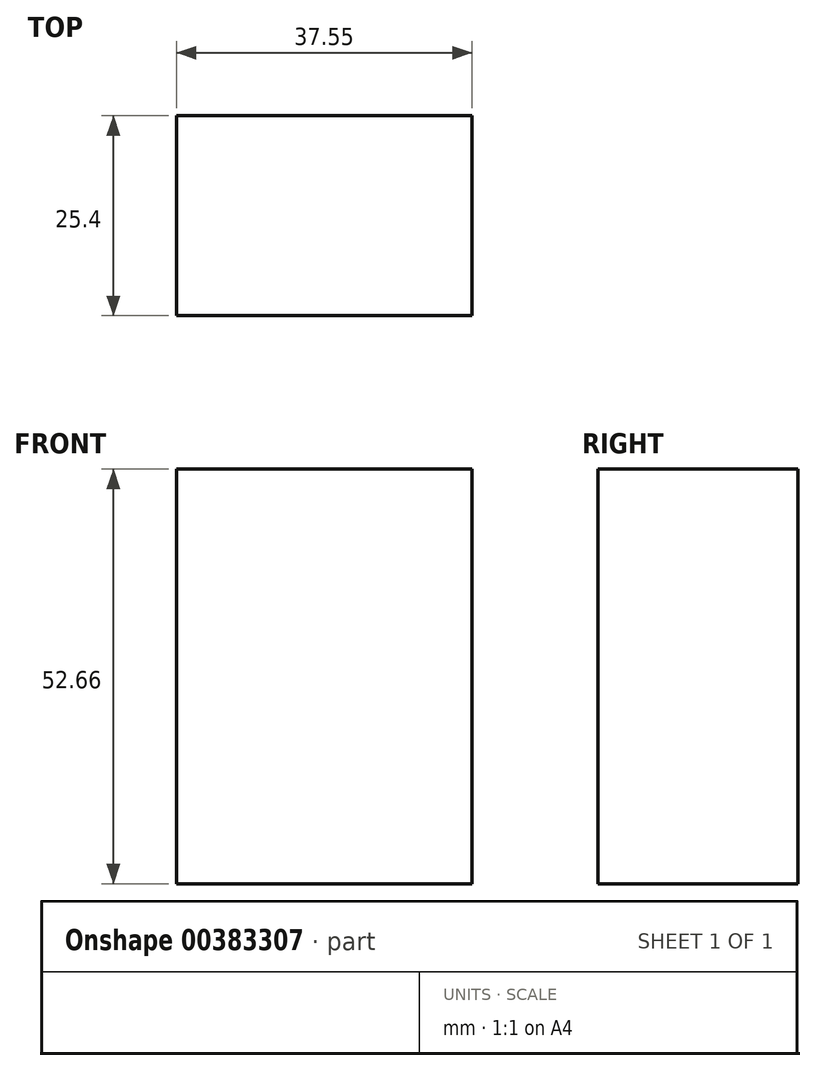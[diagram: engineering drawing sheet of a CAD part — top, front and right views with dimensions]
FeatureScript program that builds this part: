
annotation { "Feature Type Name" : "Feature", "Feature Type Description" : "" }
export const myFeature = defineFeature(function(context is Context, id is Id, definition is map)
    precondition{}
    {
        {
            var Q0;
            Q0=qCreatedBy(makeId("Front.planeOp"),FACE);
            var sketch = newSketch(context, id + "F0", { "sketchPlane" : qUnion([Q0])});
            skLineSegment(sketch, "E0.bottom", {"start": v(23.47, -21.82) * mm, "end": v(61.02, -21.82) * mm});
            skLineSegment(sketch, "E0.top", {"start": v(23.47, 30.84) * mm, "end": v(61.02, 30.84) * mm});
            skLineSegment(sketch, "E0.left", {"start": v(23.47, -21.82) * mm, "end": v(23.47, 30.84) * mm});
            skLineSegment(sketch, "E0.right", {"start": v(61.02, -21.82) * mm, "end": v(61.02, 30.84) * mm});
            skSolve(sketch);
        }
        {
            var Q0;
            Q0 = qSketchRegion(id + "F0", true);
            extrude(context, id + "F1", {"entities" : qUnion([Q0]), "depth" : 25.4 * mm});
        }
    });
